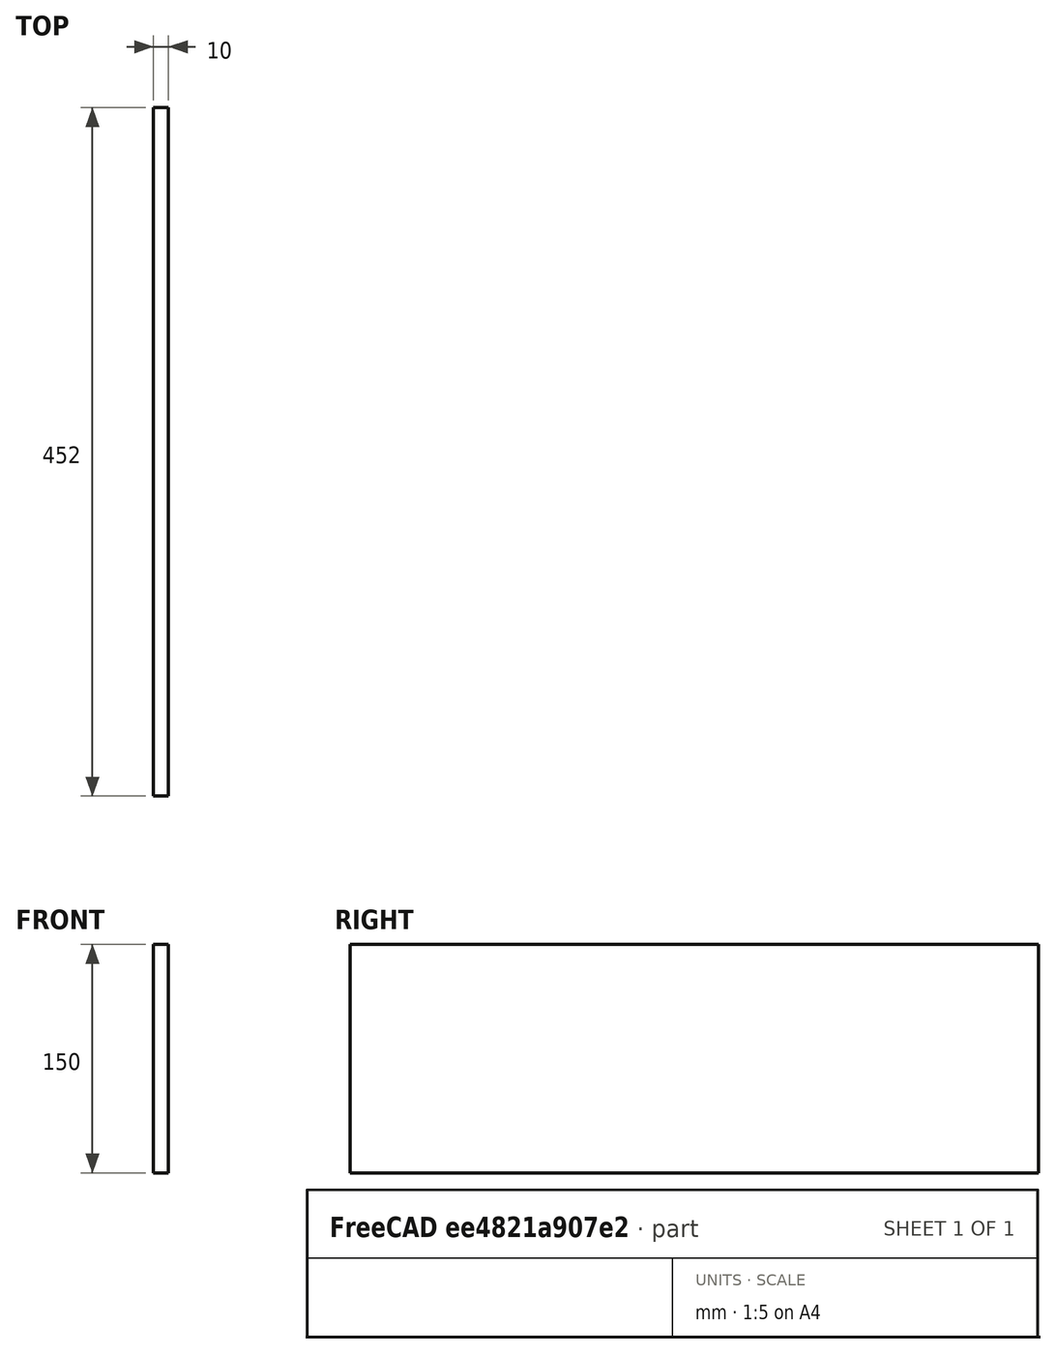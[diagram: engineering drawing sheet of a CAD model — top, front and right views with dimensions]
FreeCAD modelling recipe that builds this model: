
FCSTD DOCUMENT  (FreeCAD 0.18R16131 (Git))
Label: 500_Back_Horizontal
License: All rights reserved
LicenseURL: http://en.wikipedia.org/wiki/All_rights_reserved
objects: Sketcher::SketchObject×1, Spreadsheet::Sheet×1, PartDesign::Pad×1, PartDesign::Body×1
note: 4 computed .brp shape members not serialized (recipe doc carries the construction recipe); baked Part::Feature solids carry a one-line shape summary decoded from their .brp

FEATURE [Sketcher::SketchObject] Sketch
  MapMode = 4
  Placement = pos=(0,0,0) rot=(0.57735,0.57735,0.57735;2.0944rad)
  Support = -> [XY_Plane]
  expr: Constraints[6] = Spreadsheet.nY
  expr: Constraints[5] = Spreadsheet.nZ
  sketch-geometry (5):
    g0: LineSegment StartX=0 StartY=0 StartZ=0 EndX=0 EndY=150 EndZ=0
    g1: LineSegment StartX=452 StartY=0 StartZ=0 EndX=452 EndY=150 EndZ=0
    g2: LineSegment StartX=452 StartY=150 StartZ=0 EndX=0 EndY=150 EndZ=0
    g3: LineSegment StartX=226 StartY=0 StartZ=0 EndX=0 EndY=0 EndZ=0
    g4: LineSegment StartX=452 StartY=0 StartZ=0 EndX=226 EndY=0 EndZ=0
  constraints (14):
    c: Vertical(g0)
    c: Vertical(g1)
    c: Coincident(g2,g1)
    c: Coincident(g2,g0)
    c: Horizontal(g2)
    c: DistanceY(g1,g1) = 150
    c: DistanceX(g2,g2) = 452
    c: Coincident(g3,g0)
    c: Coincident(g4,g1)
    c: Horizontal(g4)
    c: Equal(g3,g4)
    c: Coincident(g4,g3)
    c: Horizontal(g3)
    c: Coincident(g0,g-1)
FEATURE [Spreadsheet::Sheet] Spreadsheet  label="xls"
  cells = B7=KEYBOARD FRONT; B8=Width; C8=nY; D8(nY)==500 - 19 - 19 - 10; B9=Height; C9=nZ; D9(nZ)=150; E9=F(T); B10=Thickness; C10=nT; D10(nT)=10
FEATURE [PartDesign::Pad] Pad
  Length = 10
  Length2 = 100
  Profile = -> Sketch
  Reversed = true
  Type = 0
  expr: Length = Spreadsheet.nT
FEATURE [PartDesign::Body] Body
  Group = -> [Sketch,Pad]
  Origin = -> Origin
  Tip = -> Pad
